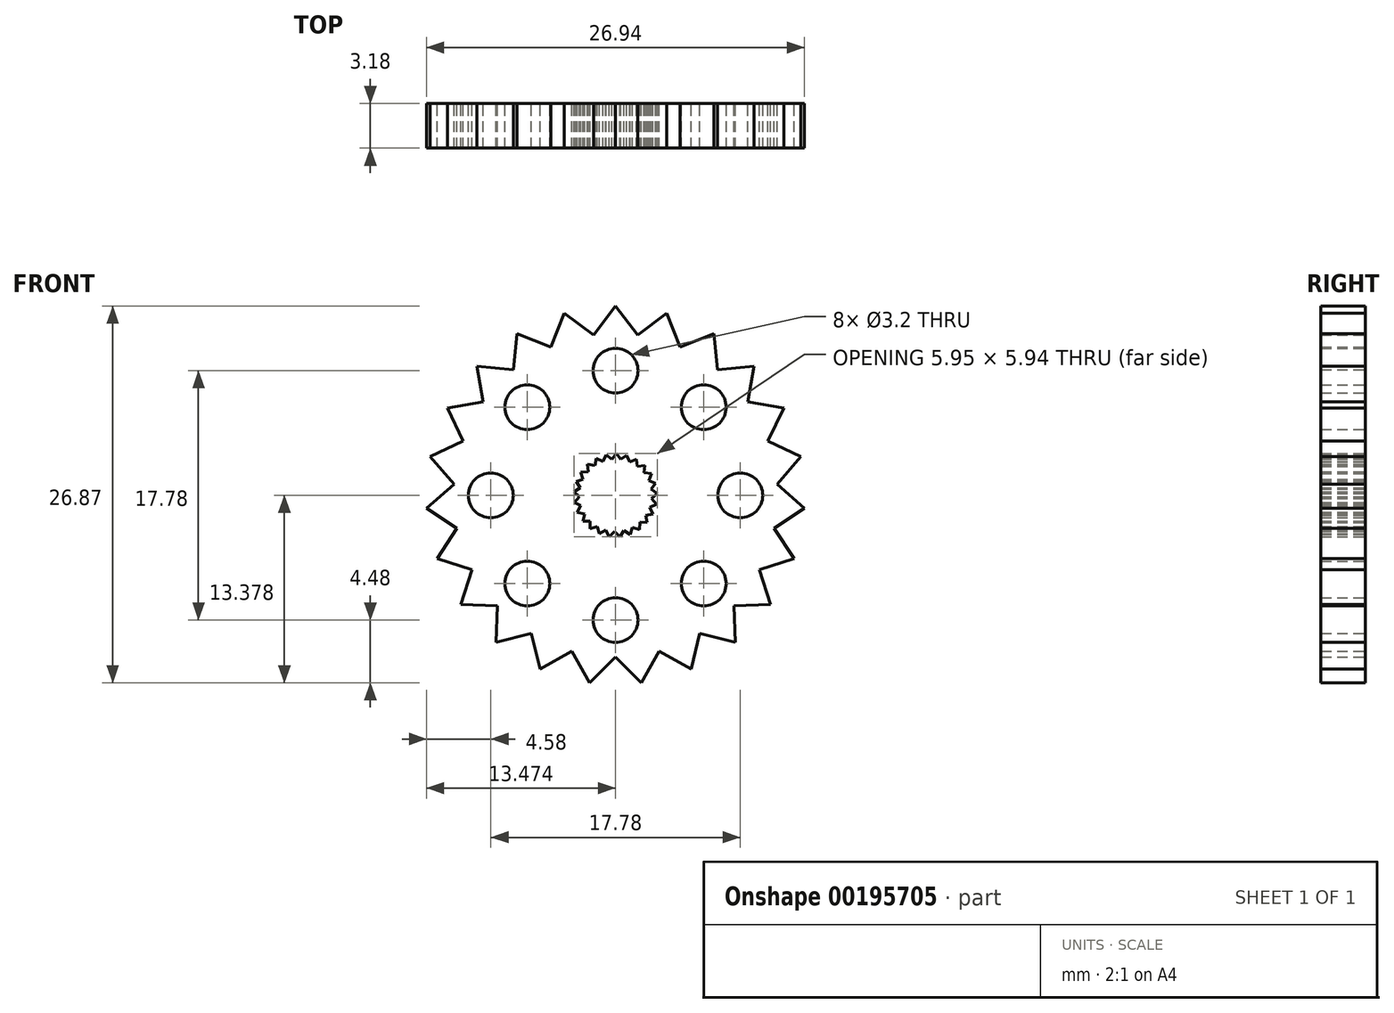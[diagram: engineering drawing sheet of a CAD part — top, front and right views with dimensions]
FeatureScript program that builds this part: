
annotation { "Feature Type Name" : "Feature", "Feature Type Description" : "" }
export const myFeature = defineFeature(function(context is Context, id is Id, definition is map)
    precondition{}
    {
        {
            var Q0;
            Q0=qCreatedBy(makeId("Front.planeOp"),FACE);
            var sketch = newSketch(context, id + "F0", { "sketchPlane" : qUnion([Q0])});
            skLineSegment(sketch, "E0", {"start": v(-2.48, 1.65) * mm, "end": v(-2.31, 1.15) * mm});
            skLineSegment(sketch, "E1", {"start": v(-2.31, 1.15) * mm, "end": v(-2.81, 0.98) * mm});
            skLineSegment(sketch, "E2.1.0", {"start": v(-2.81, 0.98) * mm, "end": v(-2.53, 0.54) * mm});
            skLineSegment(sketch, "E2.1.1", {"start": v(-2.53, 0.54) * mm, "end": v(-2.97, 0.25) * mm});
            skLineSegment(sketch, "E2.2.0", {"start": v(-2.97, 0.25) * mm, "end": v(-2.58, -0.1) * mm});
            skLineSegment(sketch, "E2.2.1", {"start": v(-2.58, -0.1) * mm, "end": v(-2.94, -0.5) * mm});
            skLineSegment(sketch, "E2.3.0", {"start": v(-2.94, -0.5) * mm, "end": v(-2.47, -0.74) * mm});
            skLineSegment(sketch, "E2.3.1", {"start": v(-2.47, -0.74) * mm, "end": v(-2.72, -1.2) * mm});
            skLineSegment(sketch, "E2.4.0", {"start": v(-2.72, -1.2) * mm, "end": v(-2.21, -1.34) * mm});
            skLineSegment(sketch, "E2.4.1", {"start": v(-2.21, -1.34) * mm, "end": v(-2.34, -1.85) * mm});
            skLineSegment(sketch, "E2.5.0", {"start": v(-2.34, -1.85) * mm, "end": v(-1.8, -1.84) * mm});
            skLineSegment(sketch, "E2.5.1", {"start": v(-1.8, -1.84) * mm, "end": v(-1.8, -2.37) * mm});
            skLineSegment(sketch, "E2.6.0", {"start": v(-1.8, -2.37) * mm, "end": v(-1.3, -2.24) * mm});
            skLineSegment(sketch, "E2.6.1", {"start": v(-1.3, -2.24) * mm, "end": v(-1.16, -2.75) * mm});
            skLineSegment(sketch, "E2.7.0", {"start": v(-1.16, -2.75) * mm, "end": v(-0.7, -2.49) * mm});
            skLineSegment(sketch, "E2.7.1", {"start": v(-0.7, -2.49) * mm, "end": v(-0.44, -2.95) * mm});
            skLineSegment(sketch, "E2.8.0", {"start": v(-0.44, -2.95) * mm, "end": v(-0.06, -2.58) * mm});
            skLineSegment(sketch, "E2.8.1", {"start": v(-0.06, -2.58) * mm, "end": v(0.3, -2.96) * mm});
            skLineSegment(sketch, "E2.9.0", {"start": v(0.3, -2.96) * mm, "end": v(0.59, -2.52) * mm});
            skLineSegment(sketch, "E2.9.1", {"start": v(0.59, -2.52) * mm, "end": v(1.04, -2.8) * mm});
            skLineSegment(sketch, "E2.10.0", {"start": v(1.04, -2.8) * mm, "end": v(1.2, -2.3) * mm});
            skLineSegment(sketch, "E2.10.1", {"start": v(1.2, -2.3) * mm, "end": v(1.7, -2.45) * mm});
            skLineSegment(sketch, "E2.11.0", {"start": v(1.7, -2.45) * mm, "end": v(1.73, -1.92) * mm});
            skLineSegment(sketch, "E2.11.1", {"start": v(1.73, -1.92) * mm, "end": v(2.25, -1.95) * mm});
            skLineSegment(sketch, "E2.12.0", {"start": v(2.25, -1.95) * mm, "end": v(2.15, -1.43) * mm});
            skLineSegment(sketch, "E2.12.1", {"start": v(2.15, -1.43) * mm, "end": v(2.67, -1.33) * mm});
            skLineSegment(sketch, "E2.13.0", {"start": v(2.67, -1.33) * mm, "end": v(2.44, -0.85) * mm});
            skLineSegment(sketch, "E2.13.1", {"start": v(2.44, -0.85) * mm, "end": v(2.91, -0.62) * mm});
            skLineSegment(sketch, "E2.14.0", {"start": v(2.91, -0.62) * mm, "end": v(2.57, -0.22) * mm});
            skLineSegment(sketch, "E2.14.1", {"start": v(2.57, -0.22) * mm, "end": v(2.98, 0.12) * mm});
            skLineSegment(sketch, "E2.15.0", {"start": v(2.98, 0.12) * mm, "end": v(2.55, 0.43) * mm});
            skLineSegment(sketch, "E2.15.1", {"start": v(2.55, 0.43) * mm, "end": v(2.85, 0.86) * mm});
            skLineSegment(sketch, "E2.16.0", {"start": v(2.85, 0.86) * mm, "end": v(2.36, 1.05) * mm});
            skLineSegment(sketch, "E2.16.1", {"start": v(2.36, 1.05) * mm, "end": v(2.55, 1.54) * mm});
            skLineSegment(sketch, "E2.17.0", {"start": v(2.55, 1.54) * mm, "end": v(2.03, 1.6) * mm});
            skLineSegment(sketch, "E2.17.1", {"start": v(2.03, 1.6) * mm, "end": v(2.09, 2.13) * mm});
            skLineSegment(sketch, "E2.18.0", {"start": v(2.09, 2.13) * mm, "end": v(1.56, 2.06) * mm});
            skLineSegment(sketch, "E2.18.1", {"start": v(1.56, 2.06) * mm, "end": v(1.5, 2.58) * mm});
            skLineSegment(sketch, "E2.19.0", {"start": v(1.5, 2.58) * mm, "end": v(1, 2.38) * mm});
            skLineSegment(sketch, "E2.19.1", {"start": v(1, 2.38) * mm, "end": v(0.8, 2.87) * mm});
            skLineSegment(sketch, "E2.20.0", {"start": v(0.8, 2.87) * mm, "end": v(0.38, 2.56) * mm});
            skLineSegment(sketch, "E2.20.1", {"start": v(0.38, 2.56) * mm, "end": v(0.07, 2.98) * mm});
            skLineSegment(sketch, "E2.21.0", {"start": v(0.07, 2.98) * mm, "end": v(-0.27, 2.57) * mm});
            skLineSegment(sketch, "E2.21.1", {"start": v(-0.27, 2.57) * mm, "end": v(-0.68, 2.9) * mm});
            skLineSegment(sketch, "E2.22.0", {"start": v(-0.68, 2.9) * mm, "end": v(-0.9, 2.42) * mm});
            skLineSegment(sketch, "E2.22.1", {"start": v(-0.9, 2.42) * mm, "end": v(-1.38, 2.64) * mm});
            skLineSegment(sketch, "E2.23.0", {"start": v(-1.38, 2.64) * mm, "end": v(-1.47, 2.12) * mm});
            skLineSegment(sketch, "E2.23.1", {"start": v(-1.47, 2.12) * mm, "end": v(-2, 2.22) * mm});
            skLineSegment(sketch, "E2.24.0", {"start": v(-2, 2.22) * mm, "end": v(-1.95, 1.69) * mm});
            skLineSegment(sketch, "E2.24.1", {"start": v(-1.95, 1.69) * mm, "end": v(-2.48, 1.65) * mm});
            skPoint(sketch, "E2.center", {"position": v(0, 0) * mm});
            skCircle(sketch, "E3", {"center": v(8.9, 0) * mm, "radius": 1.6 * mm});
            skCircle(sketch, "E4.1.0", {"center": v(6.29, 6.29) * mm, "radius": 1.6 * mm});
            skCircle(sketch, "E4.2.0", {"center": v(0, 8.9) * mm, "radius": 1.6 * mm});
            skCircle(sketch, "E4.3.0", {"center": v(-6.29, 6.29) * mm, "radius": 1.6 * mm});
            skCircle(sketch, "E4.4.0", {"center": v(-8.9, 0) * mm, "radius": 1.6 * mm});
            skCircle(sketch, "E4.5.0", {"center": v(-6.29, -6.29) * mm, "radius": 1.6 * mm});
            skCircle(sketch, "E4.6.0", {"center": v(0, -8.9) * mm, "radius": 1.6 * mm});
            skCircle(sketch, "E4.7.0", {"center": v(6.29, -6.29) * mm, "radius": 1.6 * mm});
            skLineSegment(sketch, "E5", {"start": v(0, 13.5) * mm, "end": v(1.6, 11.39) * mm});
            skLineSegment(sketch, "E6", {"start": v(0, 13.5) * mm, "end": v(-1.6, 11.39) * mm});
            skPoint(sketch, "E7.start.orphan", {"position": v(1.6, 8.9) * mm});
            skPoint(sketch, "E8.orphan", {"position": v(-1.6, 8.9) * mm});
            skLineSegment(sketch, "E9.1.0", {"start": v(-3.64, 13) * mm, "end": v(-1.53, 11.4) * mm});
            skLineSegment(sketch, "E9.1.1", {"start": v(-3.64, 13) * mm, "end": v(-4.61, 10.53) * mm});
            skLineSegment(sketch, "E9.2.0", {"start": v(-7.01, 11.53) * mm, "end": v(-4.55, 10.56) * mm});
            skLineSegment(sketch, "E9.2.1", {"start": v(-7.01, 11.53) * mm, "end": v(-7.28, 8.9) * mm});
            skLineSegment(sketch, "E9.3.0", {"start": v(-9.87, 9.21) * mm, "end": v(-7.23, 8.94) * mm});
            skLineSegment(sketch, "E9.3.1", {"start": v(-9.87, 9.21) * mm, "end": v(-9.41, 6.6) * mm});
            skLineSegment(sketch, "E9.4.0", {"start": v(-11.99, 6.21) * mm, "end": v(-9.38, 6.66) * mm});
            skLineSegment(sketch, "E9.4.1", {"start": v(-11.99, 6.21) * mm, "end": v(-10.85, 3.82) * mm});
            skLineSegment(sketch, "E9.5.0", {"start": v(-13.22, 2.75) * mm, "end": v(-10.82, 3.88) * mm});
            skLineSegment(sketch, "E9.5.1", {"start": v(-13.22, 2.75) * mm, "end": v(-11.48, 0.75) * mm});
            skLineSegment(sketch, "E9.6.0", {"start": v(-13.47, -0.92) * mm, "end": v(-11.47, 0.82) * mm});
            skLineSegment(sketch, "E9.6.1", {"start": v(-13.47, -0.92) * mm, "end": v(-11.25, -2.37) * mm});
            skLineSegment(sketch, "E9.7.0", {"start": v(-12.72, -4.52) * mm, "end": v(-11.27, -2.3) * mm});
            skLineSegment(sketch, "E9.7.1", {"start": v(-12.72, -4.52) * mm, "end": v(-10.2, -5.32) * mm});
            skLineSegment(sketch, "E9.8.0", {"start": v(-11.03, -7.79) * mm, "end": v(-10.23, -5.26) * mm});
            skLineSegment(sketch, "E9.8.1", {"start": v(-11.03, -7.79) * mm, "end": v(-8.38, -7.87) * mm});
            skLineSegment(sketch, "E9.9.0", {"start": v(-8.52, -10.47) * mm, "end": v(-8.43, -7.82) * mm});
            skLineSegment(sketch, "E9.9.1", {"start": v(-8.52, -10.47) * mm, "end": v(-5.95, -9.84) * mm});
            skLineSegment(sketch, "E9.10.0", {"start": v(-5.38, -12.38) * mm, "end": v(-6, -9.8) * mm});
            skLineSegment(sketch, "E9.10.1", {"start": v(-5.38, -12.38) * mm, "end": v(-3.07, -11.08) * mm});
            skLineSegment(sketch, "E9.11.0", {"start": v(-1.84, -13.37) * mm, "end": v(-3.14, -11.06) * mm});
            skLineSegment(sketch, "E9.11.1", {"start": v(-1.84, -13.37) * mm, "end": v(0.03, -11.5) * mm});
            skLineSegment(sketch, "E9.12.0", {"start": v(1.84, -13.37) * mm, "end": v(-0.03, -11.5) * mm});
            skLineSegment(sketch, "E9.12.1", {"start": v(1.84, -13.37) * mm, "end": v(3.14, -11.06) * mm});
            skLineSegment(sketch, "E9.13.0", {"start": v(5.38, -12.38) * mm, "end": v(3.07, -11.08) * mm});
            skLineSegment(sketch, "E9.13.1", {"start": v(5.38, -12.38) * mm, "end": v(6, -9.8) * mm});
            skLineSegment(sketch, "E9.14.0", {"start": v(8.52, -10.47) * mm, "end": v(5.95, -9.84) * mm});
            skLineSegment(sketch, "E9.14.1", {"start": v(8.52, -10.47) * mm, "end": v(8.43, -7.82) * mm});
            skLineSegment(sketch, "E9.15.0", {"start": v(11.03, -7.79) * mm, "end": v(8.38, -7.87) * mm});
            skLineSegment(sketch, "E9.15.1", {"start": v(11.03, -7.79) * mm, "end": v(10.23, -5.26) * mm});
            skLineSegment(sketch, "E9.16.0", {"start": v(12.72, -4.52) * mm, "end": v(10.2, -5.32) * mm});
            skLineSegment(sketch, "E9.16.1", {"start": v(12.72, -4.52) * mm, "end": v(11.27, -2.3) * mm});
            skLineSegment(sketch, "E9.17.0", {"start": v(13.47, -0.92) * mm, "end": v(11.25, -2.37) * mm});
            skLineSegment(sketch, "E9.17.1", {"start": v(13.47, -0.92) * mm, "end": v(11.47, 0.82) * mm});
            skLineSegment(sketch, "E9.18.0", {"start": v(13.22, 2.75) * mm, "end": v(11.48, 0.75) * mm});
            skLineSegment(sketch, "E9.18.1", {"start": v(13.22, 2.75) * mm, "end": v(10.82, 3.88) * mm});
            skLineSegment(sketch, "E9.19.0", {"start": v(11.99, 6.21) * mm, "end": v(10.85, 3.82) * mm});
            skLineSegment(sketch, "E9.19.1", {"start": v(11.99, 6.21) * mm, "end": v(9.38, 6.66) * mm});
            skLineSegment(sketch, "E9.20.0", {"start": v(9.87, 9.21) * mm, "end": v(9.41, 6.6) * mm});
            skLineSegment(sketch, "E9.20.1", {"start": v(9.87, 9.21) * mm, "end": v(7.23, 8.94) * mm});
            skLineSegment(sketch, "E9.21.0", {"start": v(7.01, 11.53) * mm, "end": v(7.28, 8.9) * mm});
            skLineSegment(sketch, "E9.21.1", {"start": v(7.01, 11.53) * mm, "end": v(4.55, 10.56) * mm});
            skLineSegment(sketch, "E9.22.0", {"start": v(3.64, 13) * mm, "end": v(4.61, 10.53) * mm});
            skLineSegment(sketch, "E9.22.1", {"start": v(3.64, 13) * mm, "end": v(1.53, 11.4) * mm});
            skSolve(sketch);
        }
        {
            var Q0;
            Q0=makeQuery(id+"F0.imprint","IMPRINT",FACE,{"disambiguationData":[TD([[makeQuery(id+"F0.imprint","IMPRINT",EDGE,{"derivedFrom":sQuery(id+"F0.wireOp",EDGE,"E0")}),-1.0]])]});
            extrude(context, id + "F1", {"entities" : qUnion([Q0]), "depth" : 3.17 * mm});
        }
    });
